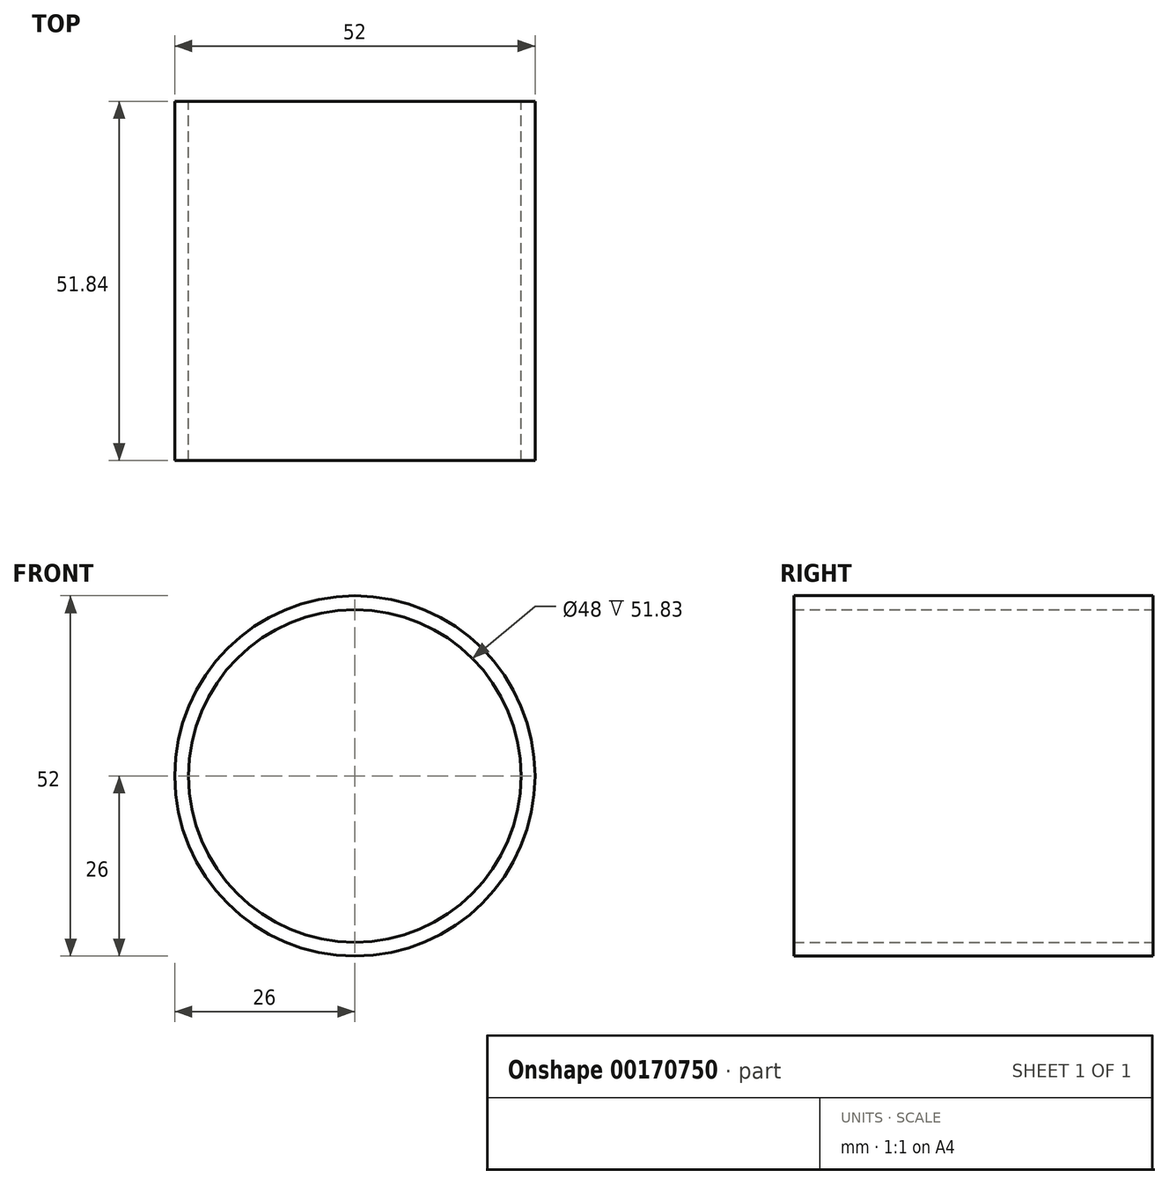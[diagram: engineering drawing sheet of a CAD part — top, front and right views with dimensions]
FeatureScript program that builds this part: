
annotation { "Feature Type Name" : "Feature", "Feature Type Description" : "" }
export const myFeature = defineFeature(function(context is Context, id is Id, definition is map)
    precondition{}
    {
        {
            var Q0;
            Q0=qCreatedBy(makeId("Front.planeOp"),FACE);
            var sketch = newSketch(context, id + "F0", { "sketchPlane" : qUnion([Q0])});
            skCircle(sketch, "E0", {"center": v(0, 0) * mm, "radius": 26 * mm});
            skCircle(sketch, "E1", {"center": v(0, 0) * mm, "radius": 24 * mm});
            skSolve(sketch);
        }
        {
            var Q0;
            Q0=qSketchRegion(id+"F0",true);
            extrude(context, id + "F1", {"entities" : qUnion([Q0]), "flatOperationType" : FlatOperationType.REMOVE, "offsetDistance" : 25 * mm, "depth" : 51.83 * mm, "domain" : OperationDomain.MODEL, "symmetric" : true});
        }
    });
